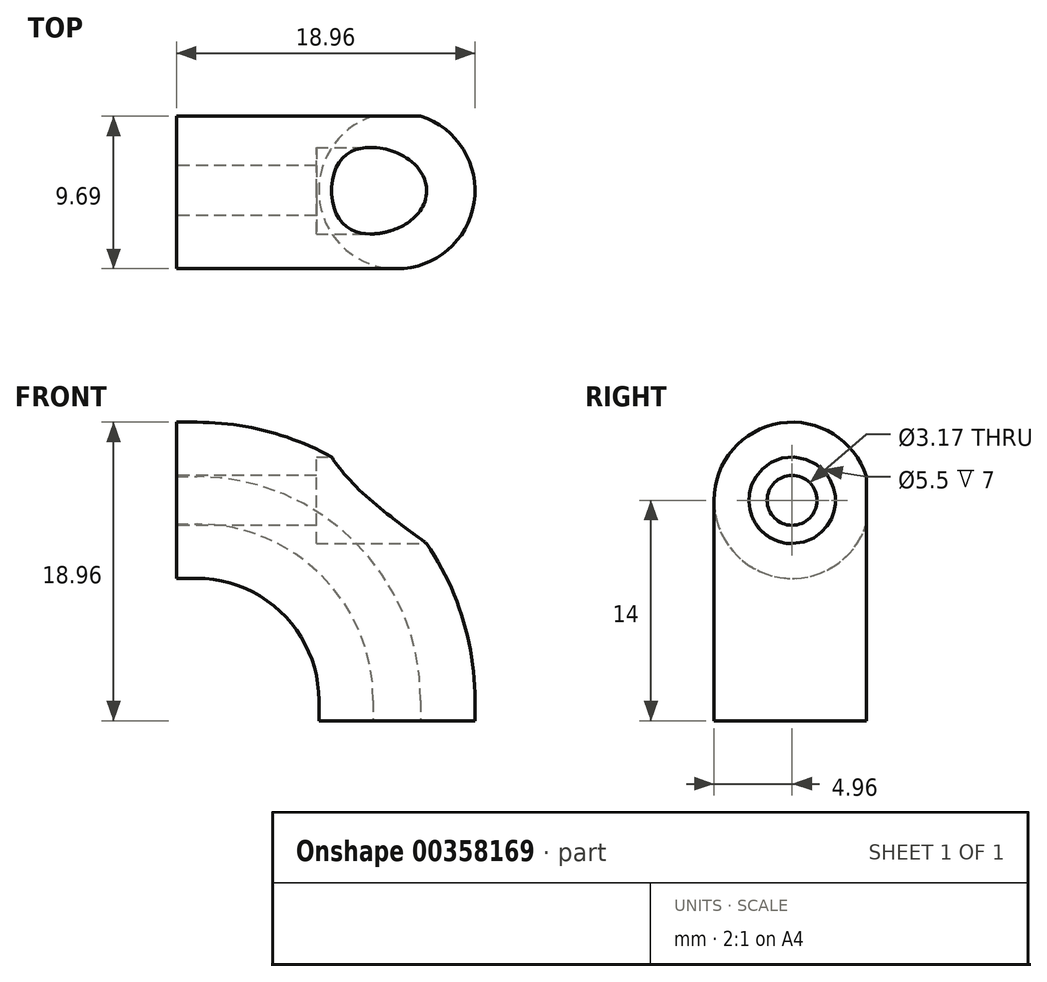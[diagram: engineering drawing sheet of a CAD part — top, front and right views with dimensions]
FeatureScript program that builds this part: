
annotation { "Feature Type Name" : "Feature", "Feature Type Description" : "" }
export const myFeature = defineFeature(function(context is Context, id is Id, definition is map)
    precondition{}
    {
        {
            var Q0;
            Q0=qCreatedBy(makeId("Front.planeOp"),FACE);
            var sketch = newSketch(context, id + "F0", { "sketchPlane" : qUnion([Q0])});
            skLineSegment(sketch, "E0", {"start": v(0, 0) * mm, "end": v(1.3, 0) * mm});
            skLineSegment(sketch, "E1", {"start": v(14, -12.7) * mm, "end": v(14, -14) * mm});
            skPoint(sketch, "E2.visualSharp", {"position": v(14, 0) * mm});
            skArc(sketch, "E2.filletArc", {"start": v(14, -12.7) * mm, "mid": v(10.28, -3.72) * mm, "end": v(1.3, 0) * mm});
            skSolve(sketch);
        }
        {
            var Q0;
            Q0=qCreatedBy(makeId("Right.planeOp"),FACE);
            var sketch = newSketch(context, id + "F1", { "sketchPlane" : qUnion([Q0])});
            skCircle(sketch, "E3", {"center": v(0, 0) * mm, "radius": 4.96 * mm});
            skSolve(sketch);
        }
        {
            var Q0;
            Q0=makeQuery(id+"F1.imprint","IMPRINT",FACE,{"disambiguationData":[TD([[makeQuery(id+"F1.imprint","IMPRINT",EDGE,{"derivedFrom":sQuery(id+"F1.wireOp",EDGE,"E3")}),1.0]])]});
            var Q1;
            Q1=sQuery(id+"F0.wireOp",EDGE,"E0");
            var Q2;
            Q2=sQuery(id+"F0.wireOp",EDGE,"E2.filletArc");
            var Q3;
            Q3=sQuery(id+"F0.wireOp",EDGE,"E1");
            sweep(context, id + "F2", {"profiles" : qUnion([Q0]), "path" : qUnion([Q1, Q2, Q3])});
        }
        {
            var Q0;
            Q0=makeQuery(id+"F2.opSweep","CAP_FACE",FACE,{"disambiguationData":[OSD([sQuery(id+"F0.wireOp",VERTEX,"E0.start"),sQuery(id+"F1.wireOp",EDGE,"E3")])],"isStart":true});
            var sketch = newSketch(context, id + "F3", { "sketchPlane" : qUnion([Q0])});
            skCircle(sketch, "E4", {"center": v(0, 0) * mm, "radius": 1.59 * mm});
            skSolve(sketch);
        }
        {
            var Q0;
            Q0=qSketchRegion(id+"F3",true);
            extrude(context, id + "F4", {"entities" : qUnion([Q0]), "operationType" : NewBodyOperationType.REMOVE, "endBound" : BoundingType.THROUGH_ALL, "oppositeDirection" : true, "depth" : 25.4 * mm});
        }
        {
            var Q0;
            Q0=qCreatedBy(makeId("Right.planeOp"),FACE);
            cPlane(context, id + "F5", {"entities" : qUnion([Q0]), "cplaneType" : CPlaneType.OFFSET, "offset" : 19.05 * mm, "width" : 152.4 * mm, "height" : 152.4 * mm});
        }
        {
            var Q0;
            Q0=qCreatedBy(id+"F5.planeOp",FACE);
            var sketch = newSketch(context, id + "F6", { "sketchPlane" : qUnion([Q0])});
            skCircle(sketch, "E5", {"center": v(0, 0) * mm, "radius": 2.75 * mm});
            skSolve(sketch);
        }
        {
            var Q0;
            Q0=qSketchRegion(id+"F6",true);
            extrude(context, id + "F7", {"entities" : qUnion([Q0]), "operationType" : NewBodyOperationType.REMOVE, "oppositeDirection" : true, "depth" : 10.16 * mm});
        }
        {
            var Q0;
            Q0=qCreatedBy(makeId("Front.planeOp"),FACE);
            var sketch = newSketch(context, id + "F8", { "sketchPlane" : qUnion([Q0])});
            skLineSegment(sketch, "E6", {"start": v(14, -14) * mm, "end": v(14, -19.15) * mm, "construction": true});
            skLineSegment(sketch, "E7", {"start": v(14, -14) * mm, "end": v(10.19, -14) * mm});
            skArc(sketch, "E8", {"start": v(10.2, -14) * mm, "mid": v(7.6, -18.84) * mm, "end": v(9.71, -23.9) * mm});
            skArc(sketch, "E9.0", {"start": v(13.7, -15.3) * mm, "mid": v(10.34, -17.9) * mm, "end": v(11.42, -22.03) * mm});
            skLineSegment(sketch, "E10", {"start": v(13.7, -15.3) * mm, "end": v(14, -15.3) * mm});
            skLineSegment(sketch, "E11", {"start": v(11.42, -22.03) * mm, "end": v(9.71, -23.9) * mm});
            skLineSegment(sketch, "E12.MirrorCS", {"start": v(14.3, -15.3) * mm, "end": v(14, -15.3) * mm});
            skLineSegment(sketch, "E13.MirrorCS", {"start": v(14, -14) * mm, "end": v(17.8, -14) * mm});
            skArc(sketch, "E14.MirrorCS", {"start": v(17.8, -14) * mm, "mid": v(20.4, -18.84) * mm, "end": v(18.29, -23.9) * mm});
            skArc(sketch, "E15.MirrorCS", {"start": v(14.3, -15.3) * mm, "mid": v(17.66, -17.9) * mm, "end": v(16.58, -22.03) * mm});
            skLineSegment(sketch, "E16.MirrorCS", {"start": v(16.58, -22.03) * mm, "end": v(18.29, -23.9) * mm});
            skSolve(sketch);
        }
        {
            var Q0;
            Q0=qCreatedBy(makeId("Right.planeOp"),FACE);
            var sketch = newSketch(context, id + "F9", { "sketchPlane" : qUnion([Q0])});
            skLineSegment(sketch, "E17.bottom", {"start": v(4.98, -14) * mm, "end": v(4.73, -14) * mm});
            skLineSegment(sketch, "E17.top", {"start": v(4.98, 5.05) * mm, "end": v(4.73, 5.05) * mm});
            skLineSegment(sketch, "E17.left", {"start": v(4.98, -14) * mm, "end": v(4.98, 5.05) * mm});
            skLineSegment(sketch, "E17.right", {"start": v(4.73, -14) * mm, "end": v(4.73, 5.05) * mm});
            skSolve(sketch);
        }
        {
            var Q0;
            Q0=qSketchRegion(id+"F9",true);
            extrude(context, id + "F10", {"entities" : qUnion([Q0]), "operationType" : NewBodyOperationType.REMOVE, "endBound" : BoundingType.THROUGH_ALL, "depth" : 25.4 * mm});
        }
    });
